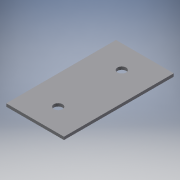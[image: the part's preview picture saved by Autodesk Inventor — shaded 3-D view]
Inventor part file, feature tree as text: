
AUTODESK INVENTOR PART (.ipt)
format: ipt  version: 2017 (Build 210142000, 142)  size: 104,960 bytes
history: native  units: in
note: dims shown in document units (in); Inventor stores cm internally (conversion verified against a paired STEP export)
features: extrude x2, sketch x2
ambient origin geometry x8: Origin, YZ Plane, XZ Plane, XY Plane, X Axis, Y Axis, Z Axis, Center Point
bodies: Solid1 (feature_tree)
feature tree (4):
  extrude  "Extrusion1"  Depth=9.5in
  extrude  "Extrusion2"  Depth=0.25in
  sketch  "Sketch1"  dims[d0=5.0in d1=9.5in]
  sketch  "Sketch2"  dims[d2=0.25in d3=0.0in d4=0.75in d5=0.75in d6=2.0in d7=2.0in d8=2.5in d9=2.5in d10=1.0in d11=0.0in]
